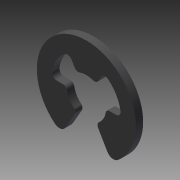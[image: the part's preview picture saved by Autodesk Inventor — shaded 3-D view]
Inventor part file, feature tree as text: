
AUTODESK INVENTOR PART (.ipt)
format: ipt  version: 2014 (Build 180170000, 170)  size: 133,120 bytes
history: native  units: in
note: dims shown in document units (in); Inventor stores cm internally (conversion verified against a paired STEP export)
features: other x7, extrude x1, sketch x1
ambient origin geometry x8: Origin, YZ Plane, XZ Plane, XY Plane, X Axis, Y Axis, Z Axis, Center Point
bodies: Solid1 (feature_tree)
feature tree (9):
  extrude  "Extrusion1"  [1 undecoded]
  other  "RR_XY"
  other  "RR_YZ"
  other  "RR_ZX"
  other  "RR_X"
  other  "RR_Y"
  other  "RR_Z"
  other  "RR_Center"
  sketch  "Sketch_1"  dims[d0=0.0275in d1=0.0in]
note: 1 required parameter value undecoded (feature->parameter linkage not recoverable at this tier; creation-order binding heuristic only, values carry confidence <= 0.55)
